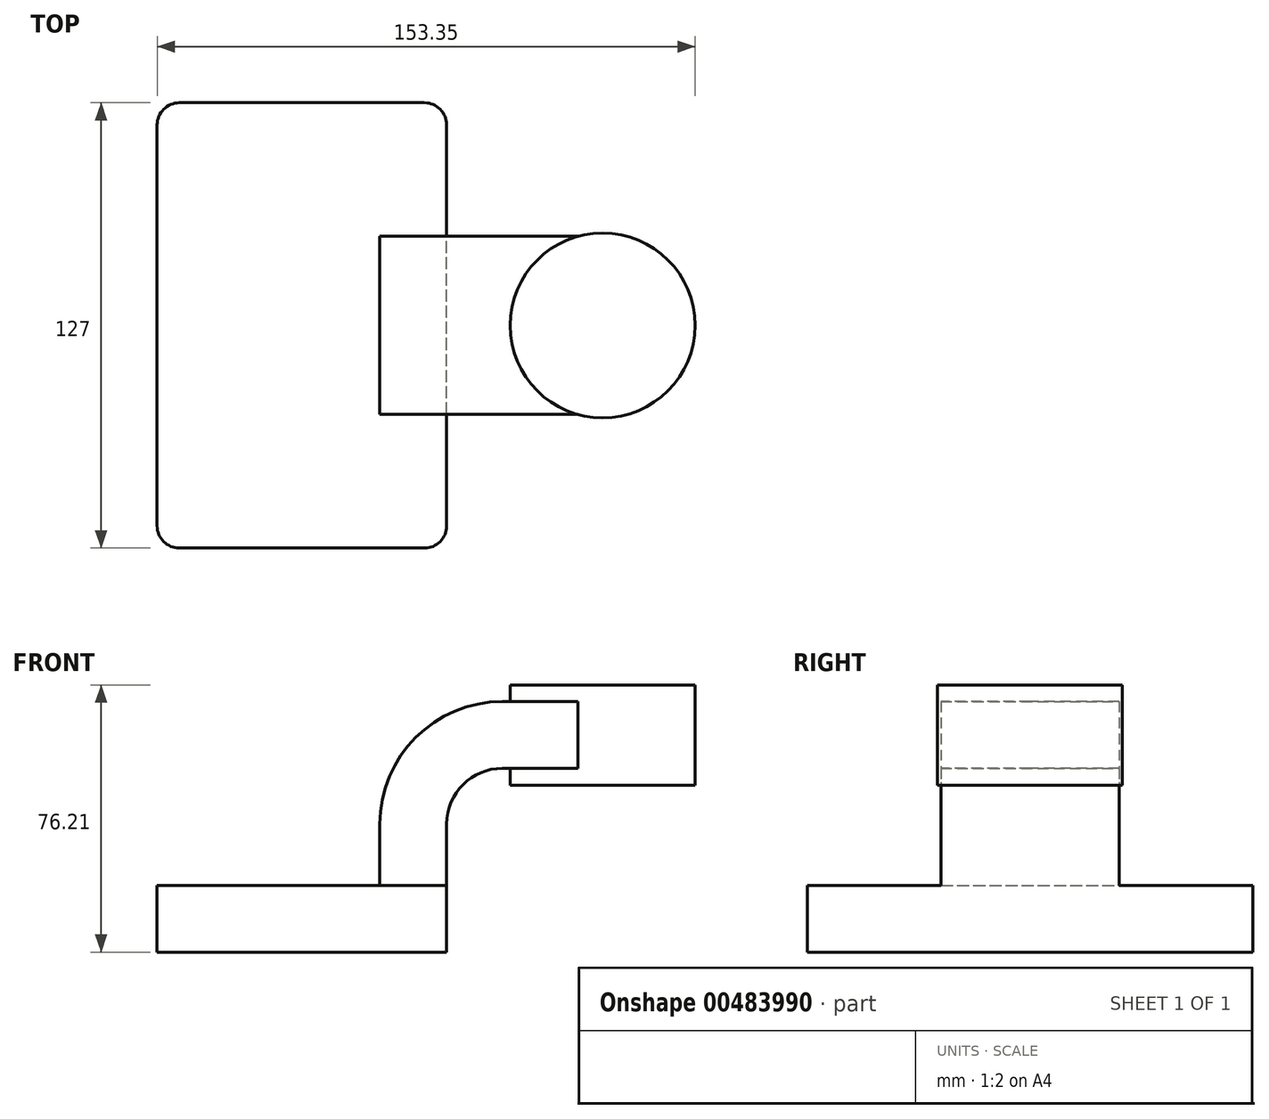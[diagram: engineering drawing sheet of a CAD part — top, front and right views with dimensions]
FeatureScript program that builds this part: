
annotation { "Feature Type Name" : "Feature", "Feature Type Description" : "" }
export const myFeature = defineFeature(function(context is Context, id is Id, definition is map)
    precondition{}
    {
        {
            var Q0;
            Q0=qCreatedBy(makeId("Front.planeOp"),FACE);
            var sketch = newSketch(context, id + "F0", { "sketchPlane" : qUnion([Q0])});
            skLineSegment(sketch, "E0.bottom", {"start": v(41.27, 9.53) * mm, "end": v(-41.28, 9.53) * mm});
            skLineSegment(sketch, "E0.top", {"start": v(41.28, -9.52) * mm, "end": v(-41.28, -9.52) * mm});
            skLineSegment(sketch, "E0.left", {"start": v(41.28, 9.53) * mm, "end": v(41.28, -9.52) * mm});
            skLineSegment(sketch, "E0.right", {"start": v(-41.28, 9.53) * mm, "end": v(-41.28, -9.52) * mm});
            skPoint(sketch, "E0.middle", {"position": v(0, 0) * mm});
            skLineSegment(sketch, "E1.bottom", {"start": v(112.08, 38.1) * mm, "end": v(61.28, 38.1) * mm});
            skLineSegment(sketch, "E1.top", {"start": v(112.08, 66.68) * mm, "end": v(61.28, 66.68) * mm});
            skLineSegment(sketch, "E1.left", {"start": v(112.08, 38.1) * mm, "end": v(112.08, 66.68) * mm});
            skLineSegment(sketch, "E1.right", {"start": v(61.28, 38.1) * mm, "end": v(61.28, 66.68) * mm});
            skPoint(sketch, "E1.middle", {"position": v(86.68, 52.39) * mm});
            skLineSegment(sketch, "E2", {"start": v(41.27, 9.53) * mm, "end": v(41.27, 27) * mm});
            skArc(sketch, "E3", {"start": v(41.27, 27) * mm, "mid": v(45.92, 38.23) * mm, "end": v(57.15, 42.88) * mm});
            skLineSegment(sketch, "E4", {"start": v(57.15, 42.88) * mm, "end": v(85.72, 42.88) * mm});
            skLineSegment(sketch, "E5.0", {"start": v(57.15, 61.93) * mm, "end": v(85.72, 61.93) * mm});
            skArc(sketch, "E5.1", {"start": v(22.23, 27) * mm, "mid": v(32.45, 51.7) * mm, "end": v(57.15, 61.93) * mm});
            skLineSegment(sketch, "E5.2", {"start": v(22.23, 9.53) * mm, "end": v(22.22, 27) * mm});
            skLineSegment(sketch, "E6", {"start": v(85.72, 38.1) * mm, "end": v(85.72, 66.68) * mm});
            skFitSpline(sketch, "E7", {"points": [v(-41.28, 9.53) * mm, v(57.15, 61.93) * mm], "startDerivative": vector(6.98, 56.92) * mm, "endDerivative": vector(171.45, -1.34) * mm});
            skSolve(sketch);
        }
        {
            var Q0;
            Q0=makeQuery(id+"F0.imprint","IMPRINT",FACE,{"disambiguationData":[TD([[makeQuery(id+"F0.imprint","IMPRINT",EDGE,{"derivedFrom":sQuery(id+"F0.wireOp",EDGE,"E0.top")}),-1.0]])]});
            extrude(context, id + "F1", {"entities" : qUnion([Q0]), "endBound" : BoundingType.SYMMETRIC, "depth" : 127 * mm, "offsetDistance" : 25.4 * mm});
        }
        {
            var Q0;
            {var subQ1=sQuery(id+"F0.wireOp",EDGE,"E2");Q0=makeQuery(id+"F0.imprint","IMPRINT",FACE,{"disambiguationData":[TD([[makeQuery(id+"F0.imprint","IMPRINT",EDGE,{"derivedFrom":subQ1}),1.0]])]});}
            var Q1;
            {var subQ0=sQuery(id+"F0.wireOp",EDGE,"E4");var subQ1=sQuery(id+"F0.wireOp",EDGE,"E1.right");var subQ2=makeQuery(id+"F0.imprint","INTERSECT",VERTEX,{"derivedFrom":[subQ1,subQ0]});Q1=makeQuery(id+"F0.imprint","IMPRINT",FACE,{"disambiguationData":[TD([[makeQuery(id+"F0.imprint","IMPRINT",EDGE,{"disambiguationData":[TD([[subQ2,-1.0]])],"derivedFrom":subQ1}),-1.0]])]});}
            extrude(context, id + "F2", {"entities" : qUnion([Q0, Q1]), "operationType" : NewBodyOperationType.ADD, "endBound" : BoundingType.SYMMETRIC, "depth" : 50.8 * mm, "offsetDistance" : 25.4 * mm});
        }
        {
            var Q0;
            Q0=makeQuery(id+"F0.imprint","IMPRINT",FACE,{"disambiguationData":[TD([[makeQuery(id+"F0.imprint","IMPRINT",EDGE,{"derivedFrom":sQuery(id+"F0.wireOp",EDGE,"E5.1")}),1.0]])]});
            extrude(context, id + "F3", {"entities" : qUnion([Q0]), "operationType" : NewBodyOperationType.ADD, "endBound" : BoundingType.SYMMETRIC, "depth" : 15.88 * mm, "offsetDistance" : 25.4 * mm});
        }
        {
            var Q0;
            {var subQ4=sQuery(id+"F0.wireOp",EDGE,"E1.left");Q0=makeQuery(id+"F0.imprint","IMPRINT",FACE,{"disambiguationData":[TD([[makeQuery(id+"F0.imprint","IMPRINT",EDGE,{"derivedFrom":subQ4}),1.0]])]});}
            var Q1;
            Q1=sQuery(id+"F0.wireOp",EDGE,"E6");
            revolve(context, id + "F4", {"operationType" : NewBodyOperationType.ADD, "surfaceOperationType" : NewSurfaceOperationType.NEW, "entities" : qUnion([Q0]), "axis" : qUnion([Q1]), "revolveType" : RevolveType.FULL});
        }
        {
            var Q0;
            Q0=makeQuery(id+"F1.opExtrude","CAP_EDGE",EDGE,{"disambiguationData":[OSD([sQuery(id+"F0.wireOp",EDGE,"E0.left")])],"isStart":false});
            var Q1;
            Q1=makeQuery(id+"F1.opExtrude","CAP_EDGE",EDGE,{"disambiguationData":[OSD([sQuery(id+"F0.wireOp",EDGE,"E0.right")])],"isStart":false});
            var Q2;
            Q2=makeQuery(id+"F1.opExtrude","CAP_EDGE",EDGE,{"disambiguationData":[OSD([sQuery(id+"F0.wireOp",EDGE,"E0.right")])],"isStart":true});
            var Q3;
            Q3=makeQuery(id+"F1.opExtrude","CAP_EDGE",EDGE,{"disambiguationData":[OSD([sQuery(id+"F0.wireOp",EDGE,"E0.left")])],"isStart":true});
            fillet(context, id + "F5", {"entities" : qUnion([Q0, Q1, Q2, Q3]), "radius" : 6.35 * mm, "tangentPropagation" : true, "allowEdgeOverflow" : false});
        }
    });
